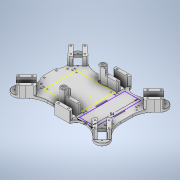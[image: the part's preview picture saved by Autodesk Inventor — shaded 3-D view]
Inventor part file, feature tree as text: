
AUTODESK INVENTOR PART (.ipt)
format: ipt  version: 2020.3 (Build 243373000, 373)  size: 1,449,984 bytes
history: native  units: mm
features: sketch x9, extrude x9, fillet x8, hole x7, projected_geometry x2, plane x1
ambient origin geometry x8: Origin, YZ Plane, XZ Plane, XY Plane, X Axis, Y Axis, Z Axis, Center Point
bodies: Body1 (feature_tree)
feature tree (36):
  sketch  "Sketch1"  dims[d0=135.0deg d4=24.6mm]
  extrude  "Extrusion10"  Depth=24.6mm
  extrude  "Extrusion11"  Depth=70.0mm
  extrude  "Extrusion12"  Depth=8.7mm
  sketch  "Sketch12"  dims[d53=1.5mm d54=20.0mm d59=1.0mm d60=90.0mm d61=135.0deg d70=135.0deg d82=0.7mm d83=0.7mm d84=0.7mm d85=0.7mm d86=6.0mm d87=5.0mm d88=0.0mm d89=20.92mm d90=0.0mm d91=1.9mm d92=6.0mm d93=4.2mm d94=2.0mm d95=90.0deg d96=8.0mm d97=0.0mm d98=2.0mm d99=1.0mm d100=2.0mm d101=0.5mm d103=0.5mm d104=0.5mm d105=18.0mm d108=3.0mm d110=2.9mm d111=6.0mm d112=4.0mm d113=2.0mm d114=90.0deg d115=4.3mm d116=0.0mm d117=30.0mm d119=84.0mm d120=1.9mm d121=6.0mm d122=4.0mm d123=2.0mm d124=90.0deg d125=8.0mm d126=0.0mm d128=12.0mm d129=2.094395mm d130=6.0mm d134=32.32mm d135=0.0mm d136=0.3mm d137=5.6mm d138=6.0mm d139=9.0mm d140=1.1mm d141=90.0deg d142=6.6mm d143=0.0mm d144=0.2mm d145=1.0mm d146=1.5mm d147=10.0mm d148=0.0mm d149=0.0mm d150=1.0mm d151=10.0mm d152=1.5mm d153=10.0mm d154=0.0mm d155=1.0mm d156=10.0mm d158=1.5mm d159=10.0mm d160=0.0mm d161=1.0mm d162=10.0mm d163=1.5mm d164=10.0mm d165=0.0mm d166=2.0mm d173=0.5mm d174=4.0mm d175=1.0mm d176=3.0mm d177=0.5mm d178=9.7mm d179=4.0mm d181=0.2mm d182=6.0mm d183=4.0mm d185=21.842mm d186=0.0mm d187=0.3mm d188=24.0mm d189=52.462385mm d190=74.962385mm d191=2.0mm d192=2.0mm d193=2.0mm d194=2.1mm d195=6.0mm d196=4.0mm d197=2.0mm d198=90.0deg d199=7.3mm d200=0.0mm d201=10.0mm d204=30.0deg d205=25.0mm d206=5.0mm d207=0.0mm d210=15.0mm d211=10.0mm d213=15.0mm d214=4.0mm d215=22.856406mm d216=3.0mm d217=45.0mm d218=3.0mm d219=6.0mm d220=6.5mm d221=2.0mm d222=90.0deg d223=8.0mm d224=20.594885mm d225=3.0mm d226=6.0mm d227=6.5mm d228=2.0mm d229=90.0deg d230=8.0mm d231=20.594885mm]
  extrude  "Extrusion19"  Depth=6.0mm
  hole  "Hole1"  [1 undecoded]
  fillet  "Fillet8"  Radius=20.0mm
  fillet  "Fillet9"  Radius=6.0mm
  fillet  "Fillet11"  Radius=135.0mm
  fillet  "Fillet12"  Radius=15.0mm
  fillet  "Fillet14"  Radius=4.0mm
  sketch  "Sketch2"  dims[d5=12.4mm d6=70.0mm]
  hole  "Hole2"  [1 undecoded]
  sketch  "Sketch3"  dims[d7=60.0mm d9=8.7mm]
  hole  "Hole3"  [1 undecoded]
  fillet  "Fillet13"  Radius=84.0mm
  extrude  "Extrusion13"  Depth=3.0mm
  extrude  "Extrusion14"  Depth=10.0mm
  extrude  "Extrusion15"  Depth=10.0mm
  extrude  "Extrusion16"  Depth=10.0mm
  plane  "Work Plane1"
  hole  "Hole4"  [1 undecoded]
  extrude  "Extrusion18"  TaperAngle=135.0deg  [1 undecoded]
  fillet  "Fillet15"  Radius=0.7mm
  fillet  "Fillet16"  Radius=0.7mm
  hole  "Hole5"  [1 undecoded]
  sketch  "Sketch11"  dims[d51=3.0mm d52=3.0mm]
  hole  "Hole6"  [1 undecoded]
  hole  "Hole7"  [1 undecoded]
  sketch  "Sketch4"  dims[d10=135.0deg d12=6.0mm]
  sketch  "Sketch6"  dims[d13=2.0mm d14=2.0mm d16=20.0mm d23=6.0mm d29=135.0mm d32=15.0mm d33=4.0mm]
  projected_geometry  "Projected Loop1"
  sketch  "Sketch8"  dims[d34=28.4mm d38=4.0mm]
  sketch  "Sketch10"  dims[d40=6.8mm d49=30.0mm d50=84.0mm]
  projected_geometry  "Project Cut Edges4"
note: 8 required parameter values undecoded (feature->parameter linkage not recoverable at this tier; creation-order binding heuristic only, values carry confidence <= 0.55)
